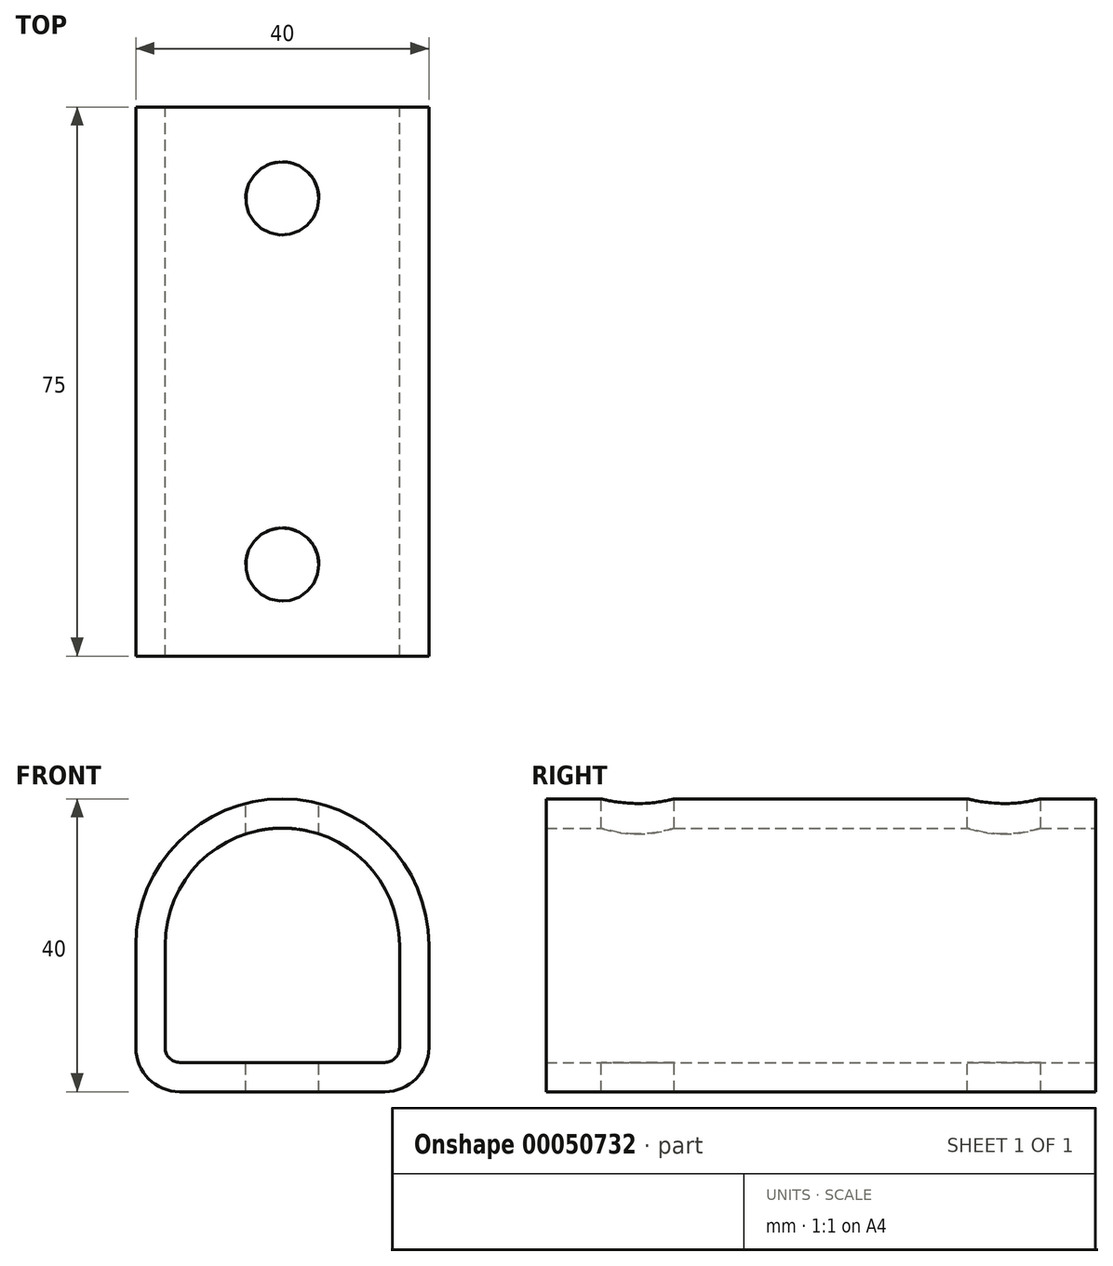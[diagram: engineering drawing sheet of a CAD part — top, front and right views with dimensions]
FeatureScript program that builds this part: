
annotation { "Feature Type Name" : "Feature", "Feature Type Description" : "" }
export const myFeature = defineFeature(function(context is Context, id is Id, definition is map)
    precondition{}
    {
        {
            var Q0;
            Q0=qCreatedBy(makeId("Front.planeOp"),FACE);
            var sketch = newSketch(context, id + "F0", { "sketchPlane" : qUnion([Q0])});
            skLineSegment(sketch, "E0.rect.bottom", {"start": v(20, -20) * mm, "end": v(-20, -20) * mm});
            skLineSegment(sketch, "E0.rect.left", {"start": v(20, -20) * mm, "end": v(20, 0) * mm});
            skLineSegment(sketch, "E0.rect.right", {"start": v(-20, -20) * mm, "end": v(-20, 0) * mm});
            skPoint(sketch, "E0.rect.middle", {"position": v(0, 0) * mm});
            skArc(sketch, "E1", {"start": v(-20, 0) * mm, "mid": v(0, 20) * mm, "end": v(20, 0) * mm});
            skPoint(sketch, "E2.orphan", {"position": v(-20, 20) * mm});
            skPoint(sketch, "E3.orphan", {"position": v(20, 20) * mm});
            skSolve(sketch);
        }
        {
            var Q0;
            Q0=makeQuery(id+"F0.imprint","IMPRINT",FACE,{"disambiguationData":[TD([[makeQuery(id+"F0.imprint","IMPRINT",EDGE,{"derivedFrom":sQuery(id+"F0.wireOp",EDGE,"E0.rect.bottom")}),-1.0]])]});
            extrude(context, id + "F1", {"entities" : qUnion([Q0]), "endBound" : BoundingType.SYMMETRIC, "depth" : 75 * mm});
        }
        {
            var Q0;
            Q0=makeQuery(id+"F1.opExtrude","SWEPT_EDGE",EDGE,{"disambiguationData":[OSD([sQuery(id+"F0.wireOp",EDGE,"E0.rect.bottom"),sQuery(id+"F0.wireOp",EDGE,"E0.rect.left")])]});
            var Q1;
            Q1=makeQuery(id+"F1.opExtrude","SWEPT_EDGE",EDGE,{"disambiguationData":[OSD([sQuery(id+"F0.wireOp",EDGE,"E0.rect.bottom"),sQuery(id+"F0.wireOp",EDGE,"E0.rect.right")])]});
            fillet(context, id + "F2", {"entities" : qUnion([Q0, Q1]), "radius" : 6 * mm, "tangentPropagation" : true, "allowEdgeOverflow" : false});
        }
        {
            var Q0;
            Q0=makeQuery(id+"F1.opExtrude","CAP_FACE",FACE,{"disambiguationData":[OSD([sQuery(id+"F0.wireOp",EDGE,"E0.rect.bottom"),sQuery(id+"F0.wireOp",EDGE,"E0.rect.left"),sQuery(id+"F0.wireOp",EDGE,"E0.rect.right"),sQuery(id+"F0.wireOp",EDGE,"E1")])],"isStart":false});
            var Q1;
            Q1=makeQuery(id+"F1.opExtrude","CAP_FACE",FACE,{"disambiguationData":[OSD([sQuery(id+"F0.wireOp",EDGE,"E0.rect.bottom"),sQuery(id+"F0.wireOp",EDGE,"E0.rect.left"),sQuery(id+"F0.wireOp",EDGE,"E0.rect.right"),sQuery(id+"F0.wireOp",EDGE,"E1")])],"isStart":true});
            shell(context, id + "F3", {"entities" : qUnion([Q0, Q1]), "thickness" : 4 * mm});
        }
        {
            var Q0;
            Q0=qCreatedBy(makeId("Top.planeOp"),FACE);
            var sketch = newSketch(context, id + "F4", { "sketchPlane" : qUnion([Q0])});
            skCircle(sketch, "E4", {"center": v(0, 25) * mm, "radius": 5 * mm});
            skCircle(sketch, "E5", {"center": v(0, -25) * mm, "radius": 5 * mm});
            skSolve(sketch);
        }
        {
            var Q0;
            Q0=makeQuery(id+"F4.imprint","IMPRINT",FACE,{"disambiguationData":[TD([[makeQuery(id+"F4.imprint","IMPRINT",EDGE,{"derivedFrom":sQuery(id+"F4.wireOp",EDGE,"E5")}),1.0]])]});
            var Q1;
            Q1=makeQuery(id+"F4.imprint","IMPRINT",FACE,{"disambiguationData":[TD([[makeQuery(id+"F4.imprint","IMPRINT",EDGE,{"derivedFrom":sQuery(id+"F4.wireOp",EDGE,"E4")}),1.0]])]});
            extrude(context, id + "F5", {"entities" : qUnion([Q0, Q1]), "operationType" : NewBodyOperationType.REMOVE, "endBound" : BoundingType.THROUGH_ALL, "oppositeDirection" : true, "depth" : 25 * mm, "hasSecondDirection" : true, "secondDirectionBound" : SecondDirectionBoundingType.THROUGH_ALL, "secondDirectionOppositeDirection" : false, "secondDirectionDepth" : 25 * mm});
        }
    });
